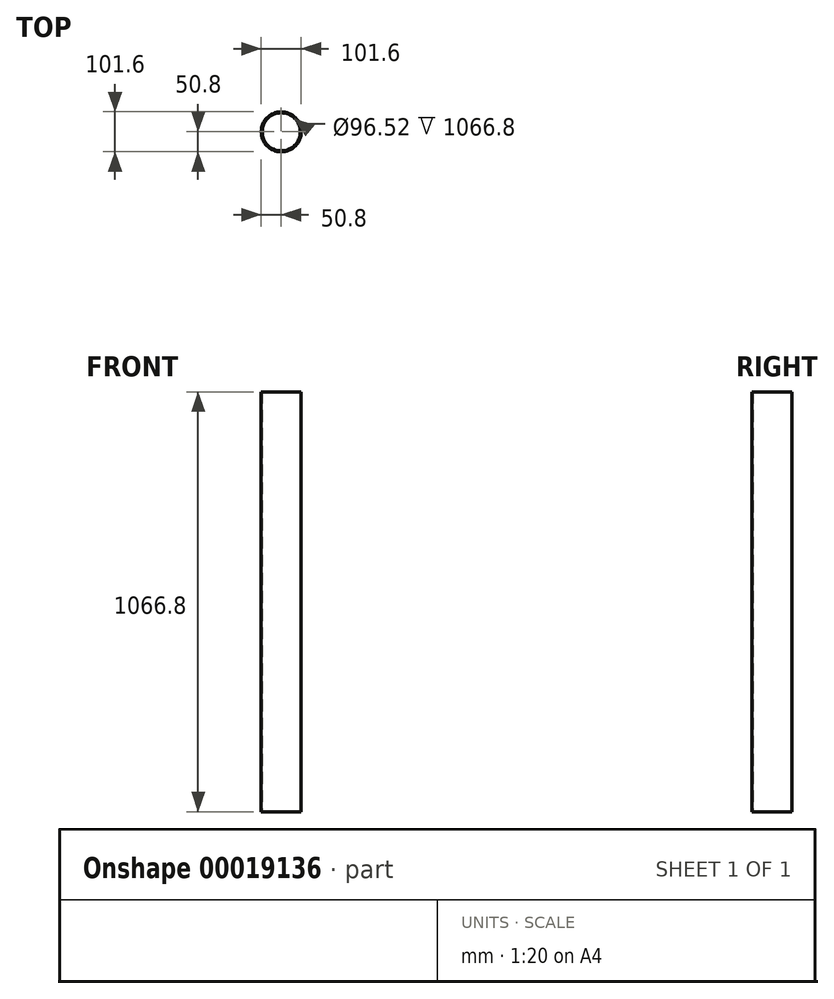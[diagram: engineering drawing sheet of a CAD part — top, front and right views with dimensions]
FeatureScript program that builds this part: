
annotation { "Feature Type Name" : "Feature", "Feature Type Description" : "" }
export const myFeature = defineFeature(function(context is Context, id is Id, definition is map)
    precondition{}
    {
        {
            var Q0;
            Q0=qCreatedBy(makeId("Top.planeOp"),FACE);
            var sketch = newSketch(context, id + "F0", { "sketchPlane" : qUnion([Q0])});
            skCircle(sketch, "E0", {"center": v(0, 0) * mm, "radius": 50.8 * mm});
            skCircle(sketch, "E1", {"center": v(0, 0) * mm, "radius": 48.26 * mm});
            skSolve(sketch);
        }
        {
            var Q0;
            Q0=makeQuery(id+"F0.imprint","IMPRINT",FACE,{"disambiguationData":[TD([[makeQuery(id+"F0.imprint","IMPRINT",EDGE,{"derivedFrom":sQuery(id+"F0.wireOp",EDGE,"E0")}),1.0]])]});
            extrude(context, id + "F1", {"entities" : qUnion([Q0]), "depth" : 1066.8 * mm});
        }
    });
